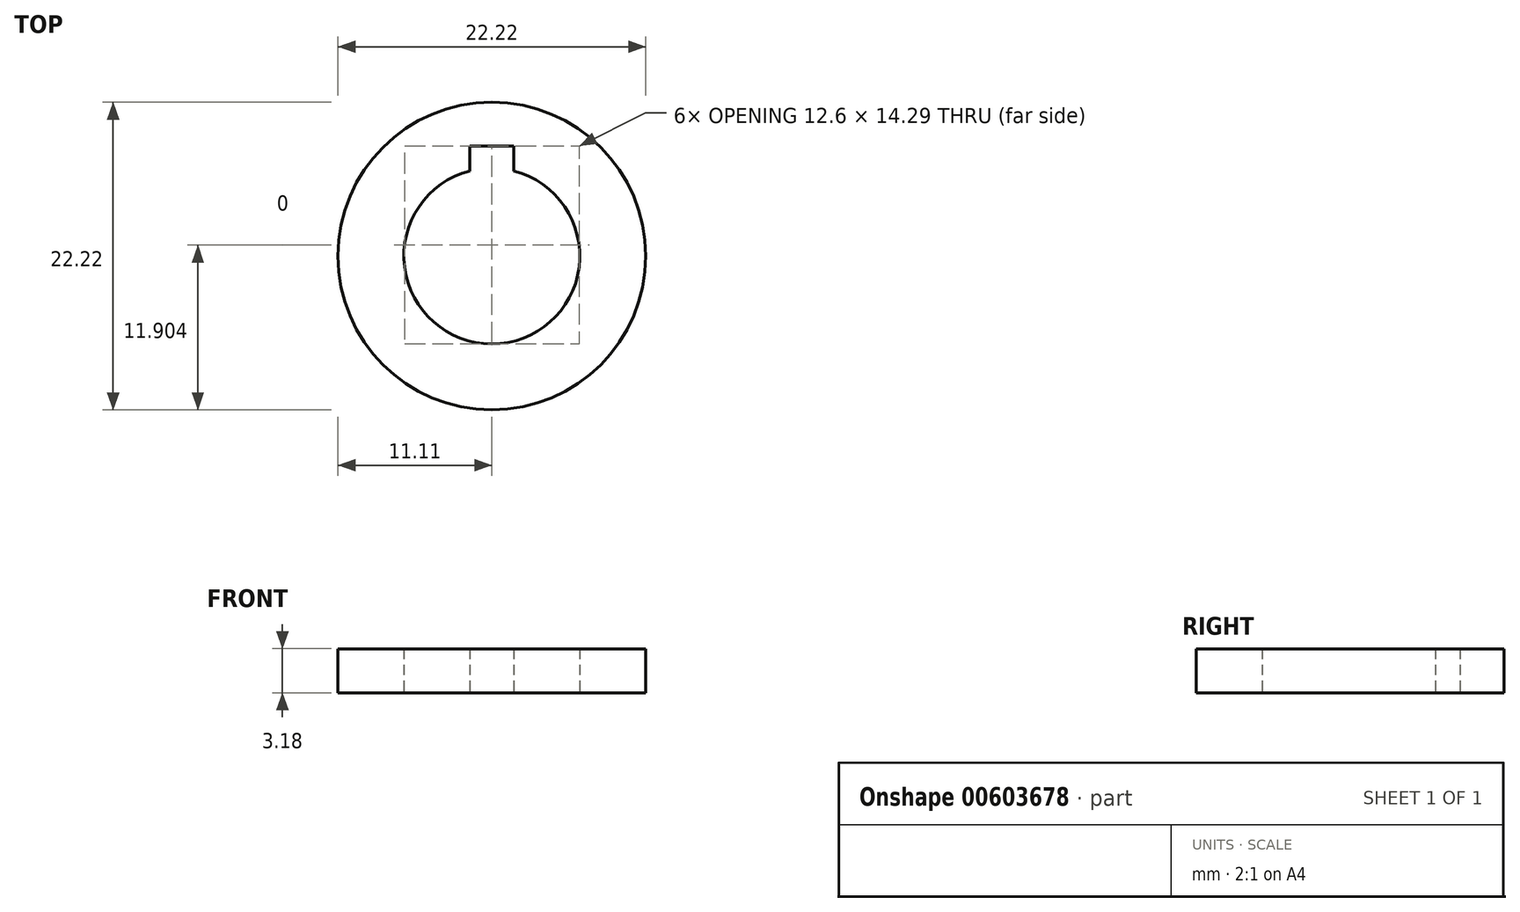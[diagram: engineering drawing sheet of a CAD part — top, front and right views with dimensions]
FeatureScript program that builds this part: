
annotation { "Feature Type Name" : "Feature", "Feature Type Description" : "" }
export const myFeature = defineFeature(function(context is Context, id is Id, definition is map)
    precondition{}
    {
        {
            var Q0;
            Q0=qCreatedBy(makeId("Top.planeOp"),FACE);
            var sketch = newSketch(context, id + "F0", { "sketchPlane" : qUnion([Q0])});
            skCircle(sketch, "E0", {"center": v(0, 0) * mm, "radius": 6.35 * mm});
            skPoint(sketch, "E1", {"position": v(0, 6.35) * mm});
            skLineSegment(sketch, "E2", {"start": v(0, 6.35) * mm, "end": v(1.59, 6.35) * mm});
            skLineSegment(sketch, "E3", {"start": v(0, 6.35) * mm, "end": v(-1.59, 6.35) * mm});
            skLineSegment(sketch, "E4", {"start": v(-1.59, 6.35) * mm, "end": v(-1.59, 7.94) * mm});
            skLineSegment(sketch, "E5", {"start": v(-1.59, 7.94) * mm, "end": v(1.59, 7.94) * mm});
            skLineSegment(sketch, "E6", {"start": v(1.59, 7.94) * mm, "end": v(1.59, 6.35) * mm});
            skLineSegment(sketch, "E7.MirrorCS", {"start": v(-1.59, 4.76) * mm, "end": v(1.59, 4.76) * mm});
            skLineSegment(sketch, "E8.MirrorCS", {"start": v(1.59, 4.76) * mm, "end": v(1.59, 6.35) * mm});
            skLineSegment(sketch, "E9.MirrorCS", {"start": v(-1.59, 6.35) * mm, "end": v(-1.59, 4.76) * mm});
            skCircle(sketch, "E10", {"center": v(0, 0) * mm, "radius": 11.11 * mm});
            skSolve(sketch);
        }
        {
            var Q0;
            Q0 = qSketchRegion(id + "F0", true);
            extrude(context, id + "F1", {"entities" : qUnion([Q0]), "depth" : 3.17 * mm, "offsetDistance" : 25.4 * mm});
        }
    });
